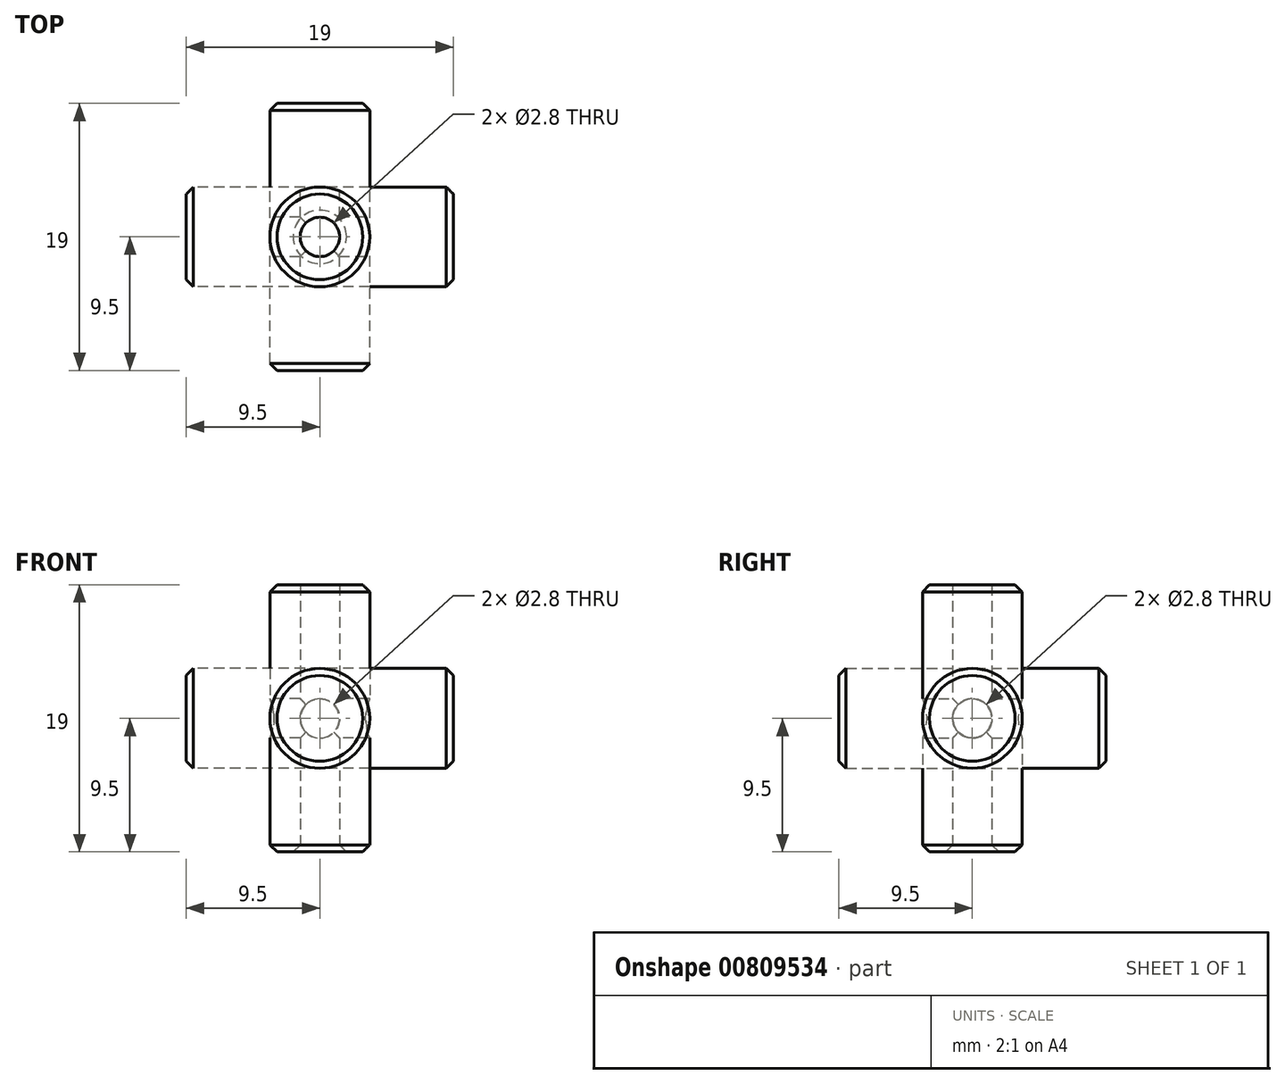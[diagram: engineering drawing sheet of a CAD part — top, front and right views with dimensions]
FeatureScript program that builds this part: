
annotation { "Feature Type Name" : "Feature", "Feature Type Description" : "" }
export const myFeature = defineFeature(function(context is Context, id is Id, definition is map)
    precondition{}
    {
        {
            var Q0;
            Q0=qCreatedBy(makeId("Front.planeOp"),FACE);
            var sketch = newSketch(context, id + "F0", { "sketchPlane" : qUnion([Q0])});
            skCircle(sketch, "E0", {"center": v(0, 0) * mm, "radius": 3.55 * mm});
            skSolve(sketch);
        }
        {
            var Q0;
            Q0 = qSketchRegion(id + "F0", true);
            extrude(context, id + "F1", {"entities" : qUnion([Q0]), "endBound" : BoundingType.SYMMETRIC, "depth" : 19 * mm, "offsetDistance" : 25 * mm});
        }
        {
            var Q0;
            Q0=qCreatedBy(makeId("Front.planeOp"),FACE);
            var sketch = newSketch(context, id + "F2", { "sketchPlane" : qUnion([Q0])});
            skCircle(sketch, "E1", {"center": v(0, 0) * mm, "radius": 1.4 * mm});
            skSolve(sketch);
        }
        {
            var Q0;
            Q0 = qSketchRegion(id + "F2", true);
            extrude(context, id + "F3", {"entities" : qUnion([Q0]), "endBound" : BoundingType.SYMMETRIC, "depth" : 20 * mm, "offsetDistance" : 25 * mm});
        }
        {
            var Q0;
            Q0=qCreatedBy(makeId("Front.planeOp"),FACE);
            var sketch = newSketch(context, id + "F4", { "sketchPlane" : qUnion([Q0])});
            skLineSegment(sketch, "E2.bottom", {"start": v(0, 0) * mm, "end": v(10, 0) * mm});
            skLineSegment(sketch, "E2.top", {"start": v(0, 10) * mm, "end": v(10, 10) * mm});
            skLineSegment(sketch, "E2.left", {"start": v(0, 0) * mm, "end": v(0, 10) * mm});
            skLineSegment(sketch, "E2.right", {"start": v(10, 0) * mm, "end": v(10, 10) * mm});
            skSolve(sketch);
        }
        {
            var Q0;
            Q0 = qSketchRegion(id + "F4", true);
            extrude(context, id + "F5", {"entities" : qUnion([Q0]), "depth" : 10 * mm, "offsetDistance" : 25 * mm});
        }
        {
            var Q0;
            Q0=qCreatedBy(makeId("Origin.pointOp"),VERTEX);
            var Q1;
            Q1=makeQuery(id+"F5.opExtrude","CAP_VERTEX",VERTEX,{"disambiguationData":[OSD([sQuery(id+"F4.wireOp",EDGE,"E2.bottom"),sQuery(id+"F4.wireOp",EDGE,"E2.right")])],"isStart":false});
            var Q2;
            Q2=makeQuery(id+"F5.opExtrude","CAP_VERTEX",VERTEX,{"disambiguationData":[OSD([sQuery(id+"F4.wireOp",EDGE,"E2.top"),sQuery(id+"F4.wireOp",EDGE,"E2.right")])],"isStart":false});
            cPlane(context, id + "F6", {"entities" : qUnion([Q0, Q1, Q2]), "cplaneType" : CPlaneType.THREE_POINT, "offset" : 25 * mm, "width" : 150 * mm, "height" : 150 * mm});
        }
        {
            var Q0;
            Q0=qCreatedBy(id+"F6.planeOp",FACE);
            var sketch = newSketch(context, id + "F7", { "sketchPlane" : qUnion([Q0])});
            skLineSegment(sketch, "E3", {"start": v(0, 0) * mm, "end": v(-14.14, 10) * mm});
            skSolve(sketch);
        }
        {
            var Q0;
            Q0=makeQuery(id+"F5.opExtrude","SWEPT_BODY",BODY,{"disambiguationData":[OSD([sQuery(id+"F4.wireOp",EDGE,"E2.bottom"),sQuery(id+"F4.wireOp",EDGE,"E2.top"),sQuery(id+"F4.wireOp",EDGE,"E2.left"),sQuery(id+"F4.wireOp",EDGE,"E2.right")])]});
            deleteBodies(context, id + "F8", {"entities" : qUnion([Q0])});
        }
        {
            var Q0;
            Q0=makeQuery(id+"F3.opExtrude","SWEPT_BODY",BODY,{"disambiguationData":[OSD([sQuery(id+"F2.wireOp",EDGE,"E1")])]});
            var Q1;
            Q1=makeQuery(id+"F1.opExtrude","SWEPT_BODY",BODY,{"disambiguationData":[OSD([sQuery(id+"F0.wireOp",EDGE,"E0")])]});
            var Q2;
            Q2=sQuery(id+"F7.wireOp",EDGE,"E3");
            circularPattern(context, id + "F9", {"entities" : qUnion([Q0, Q1]), "axis" : qUnion([Q2]), "angle" : 360 * degree, "instanceCount" : 3, "equalSpace" : true});
        }
        {
            var Q0;
            Q0=makeQuery(id+"F9.opPattern","COPY",BODY,{"derivedFrom":makeQuery(id+"F3.opExtrude","SWEPT_BODY",BODY,{"disambiguationData":[OSD([sQuery(id+"F2.wireOp",EDGE,"E1")])]}),"instanceName":"2"});
            var Q1;
            Q1=makeQuery(id+"F9.opPattern","COPY",BODY,{"derivedFrom":makeQuery(id+"F3.opExtrude","SWEPT_BODY",BODY,{"disambiguationData":[OSD([sQuery(id+"F2.wireOp",EDGE,"E1")])]}),"instanceName":"1"});
            var Q2;
            Q2=makeQuery(id+"F3.opExtrude","SWEPT_BODY",BODY,{"disambiguationData":[OSD([sQuery(id+"F2.wireOp",EDGE,"E1")])]});
            var Q3;
            Q3=makeQuery(id+"F9.opPattern","COPY",BODY,{"derivedFrom":makeQuery(id+"F1.opExtrude","SWEPT_BODY",BODY,{"disambiguationData":[OSD([sQuery(id+"F0.wireOp",EDGE,"E0")])]}),"instanceName":"2"});
            booleanBodies(context, id + "F10", {"operationType" : BooleanOperationType.SUBTRACTION, "tools" : qUnion([Q0, Q1, Q2]), "targets" : qUnion([Q3])});
        }
        {
            var Q0;
            Q0=makeQuery(id+"F9.opPattern","COPY",EDGE,{"derivedFrom":makeQuery(id+"F1.opExtrude","CAP_EDGE",EDGE,{"disambiguationData":[OSD([sQuery(id+"F0.wireOp",EDGE,"E0")])],"isStart":false}),"instanceName":"2"});
            var Q1;
            Q1=makeQuery(id+"F9.opPattern","COPY",EDGE,{"derivedFrom":makeQuery(id+"F1.opExtrude","CAP_EDGE",EDGE,{"disambiguationData":[OSD([sQuery(id+"F0.wireOp",EDGE,"E0")])],"isStart":true}),"instanceName":"1"});
            var Q2;
            Q2=makeQuery(id+"F1.opExtrude","CAP_EDGE",EDGE,{"disambiguationData":[OSD([sQuery(id+"F0.wireOp",EDGE,"E0")])],"isStart":false});
            var Q3;
            Q3=makeQuery(id+"F1.opExtrude","CAP_EDGE",EDGE,{"disambiguationData":[OSD([sQuery(id+"F0.wireOp",EDGE,"E0")])],"isStart":true});
            var Q4;
            Q4=makeQuery(id+"F9.opPattern","COPY",EDGE,{"derivedFrom":makeQuery(id+"F1.opExtrude","CAP_EDGE",EDGE,{"disambiguationData":[OSD([sQuery(id+"F0.wireOp",EDGE,"E0")])],"isStart":false}),"instanceName":"1"});
            var Q5;
            Q5=makeQuery(id+"F9.opPattern","COPY",FACE,{"derivedFrom":makeQuery(id+"F1.opExtrude","CAP_FACE",FACE,{"disambiguationData":[OSD([sQuery(id+"F0.wireOp",EDGE,"E0")])],"isStart":true}),"instanceName":"2"});
            chamfer(context, id + "F11", {"entities" : qUnion([Q0, Q1, Q2, Q3, Q4, Q5]), "width" : 0.5 * mm, "tangentPropagation" : true});
        }
    });
